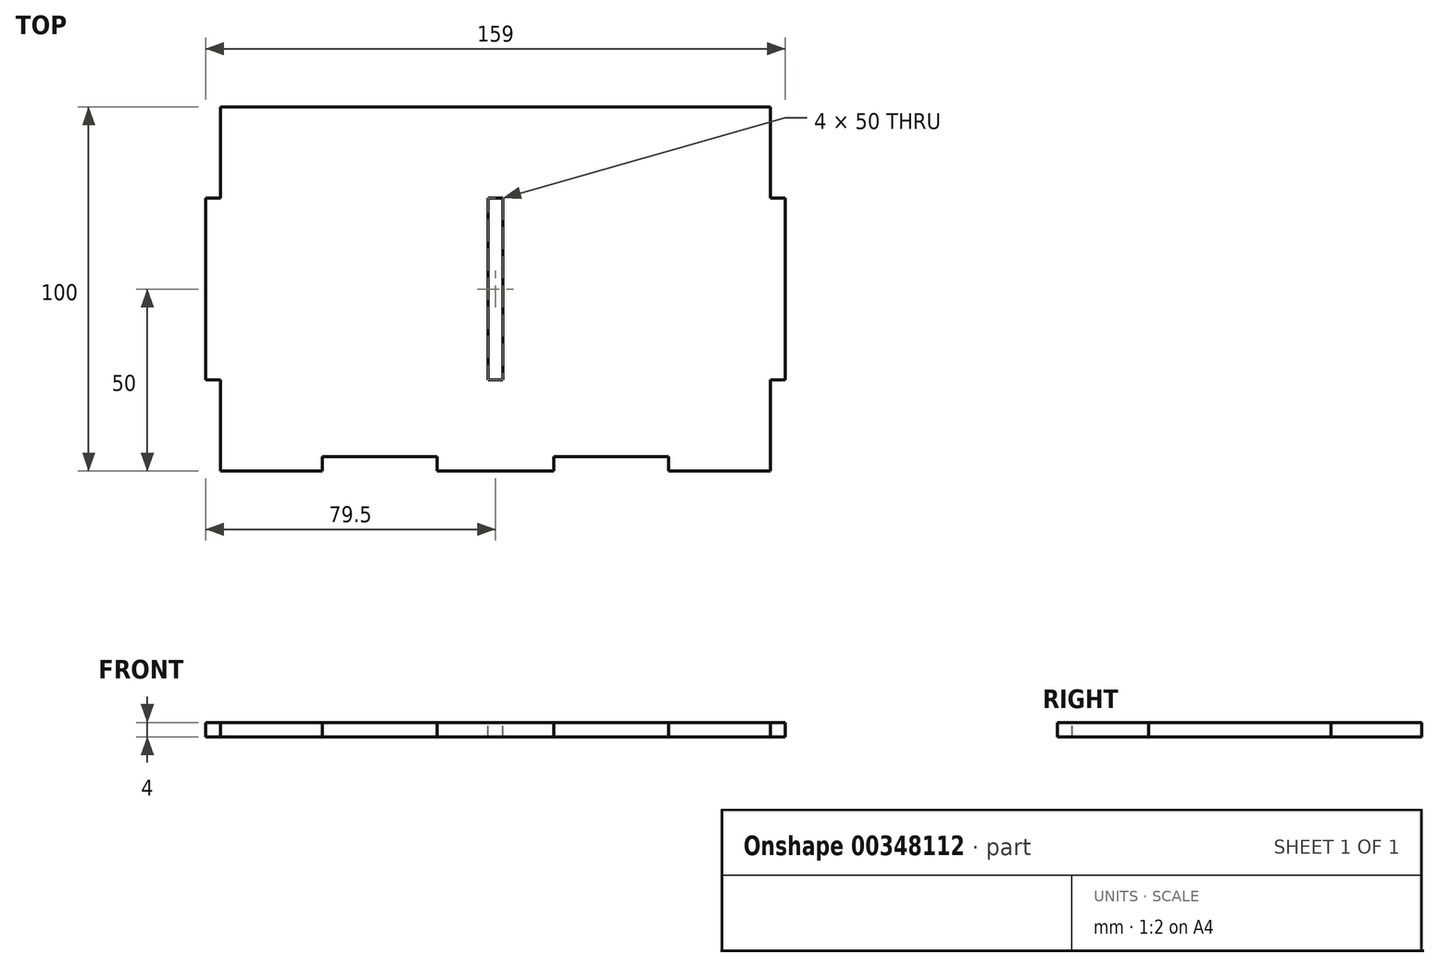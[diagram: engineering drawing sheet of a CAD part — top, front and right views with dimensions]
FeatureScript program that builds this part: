
annotation { "Feature Type Name" : "Feature", "Feature Type Description" : "" }
export const myFeature = defineFeature(function(context is Context, id is Id, definition is map)
    precondition{}
    {
        {
            var Q0;
            Q0=qCreatedBy(makeId("Top.planeOp"),FACE);
            var sketch = newSketch(context, id + "F0", { "sketchPlane" : qUnion([Q0])});
            skLineSegment(sketch, "E0.bottom", {"start": v(0, 0) * mm, "end": v(159, 0) * mm});
            skLineSegment(sketch, "E0.top", {"start": v(0, 100) * mm, "end": v(159, 100) * mm});
            skLineSegment(sketch, "E0.left", {"start": v(0, 0) * mm, "end": v(0, 100) * mm});
            skLineSegment(sketch, "E0.right", {"start": v(159, 0) * mm, "end": v(159, 100) * mm});
            skSolve(sketch);
        }
        {
            var Q0;
            Q0 = qSketchRegion(id + "F0", true);
            extrude(context, id + "F1", {"entities" : qUnion([Q0]), "depth" : 4 * mm});
        }
        {
            var Q0;
            Q0=makeQuery(id+"F1.opExtrude","CAP_FACE",FACE,{"disambiguationData":[OSD([sQuery(id+"F0.wireOp",EDGE,"E0.bottom"),sQuery(id+"F0.wireOp",EDGE,"E0.top"),sQuery(id+"F0.wireOp",EDGE,"E0.left"),sQuery(id+"F0.wireOp",EDGE,"E0.right")])],"isStart":false});
            var sketch = newSketch(context, id + "F2", { "sketchPlane" : qUnion([Q0])});
            skLineSegment(sketch, "E1.bottom", {"start": v(32, 0) * mm, "end": v(63.5, 0) * mm});
            skLineSegment(sketch, "E1.top", {"start": v(32, 4) * mm, "end": v(63.5, 4) * mm});
            skLineSegment(sketch, "E1.left", {"start": v(32, 0) * mm, "end": v(32, 4) * mm});
            skLineSegment(sketch, "E1.right", {"start": v(63.5, 0) * mm, "end": v(63.5, 4) * mm});
            skLineSegment(sketch, "E2.bottom", {"start": v(95.5, 0) * mm, "end": v(127, 0) * mm});
            skLineSegment(sketch, "E2.top", {"start": v(95.5, 4) * mm, "end": v(127, 4) * mm});
            skLineSegment(sketch, "E2.left", {"start": v(95.5, 0) * mm, "end": v(95.5, 4) * mm});
            skLineSegment(sketch, "E2.right", {"start": v(127, 0) * mm, "end": v(127, 4) * mm});
            skSolve(sketch);
        }
        {
            var Q0;
            Q0 = qSketchRegion(id + "F2", true);
            extrude(context, id + "F3", {"entities" : qUnion([Q0]), "operationType" : NewBodyOperationType.REMOVE, "endBound" : BoundingType.UP_TO_NEXT, "oppositeDirection" : true, "depth" : 25 * mm});
        }
        {
            var Q0;
            Q0=makeQuery(id+"F1.opExtrude","CAP_FACE",FACE,{"disambiguationData":[OSD([sQuery(id+"F0.wireOp",EDGE,"E0.bottom"),sQuery(id+"F0.wireOp",EDGE,"E0.top"),sQuery(id+"F0.wireOp",EDGE,"E0.left"),sQuery(id+"F0.wireOp",EDGE,"E0.right")])],"isStart":false});
            var sketch = newSketch(context, id + "F4", { "sketchPlane" : qUnion([Q0])});
            skLineSegment(sketch, "E3.bottom", {"start": v(159, 0) * mm, "end": v(155, 0) * mm});
            skLineSegment(sketch, "E3.top", {"start": v(159, 25) * mm, "end": v(155, 25) * mm});
            skLineSegment(sketch, "E3.left", {"start": v(159, 0) * mm, "end": v(159, 25) * mm});
            skLineSegment(sketch, "E3.right", {"start": v(155, 0) * mm, "end": v(155, 25) * mm});
            skLineSegment(sketch, "E4.bottom", {"start": v(159, 100) * mm, "end": v(155, 100) * mm});
            skLineSegment(sketch, "E4.top", {"start": v(159, 75) * mm, "end": v(155, 75) * mm});
            skLineSegment(sketch, "E4.left", {"start": v(159, 100) * mm, "end": v(159, 75) * mm});
            skLineSegment(sketch, "E4.right", {"start": v(155, 100) * mm, "end": v(155, 75) * mm});
            skLineSegment(sketch, "E5", {"start": v(79.5, 0) * mm, "end": v(79.5, 100) * mm, "construction": true});
            skLineSegment(sketch, "E6.MirrorCS", {"start": v(0, 75) * mm, "end": v(4, 75) * mm});
            skLineSegment(sketch, "E7.MirrorCS", {"start": v(0, 25) * mm, "end": v(4, 25) * mm});
            skLineSegment(sketch, "E8.MirrorCS", {"start": v(0, 0) * mm, "end": v(4, 0) * mm});
            skLineSegment(sketch, "E9.MirrorCS", {"start": v(0, 100) * mm, "end": v(4, 100) * mm});
            skLineSegment(sketch, "E10.MirrorCS", {"start": v(0, 100) * mm, "end": v(0, 75) * mm});
            skLineSegment(sketch, "E11.MirrorCS", {"start": v(4, 100) * mm, "end": v(4, 75) * mm});
            skLineSegment(sketch, "E12.MirrorCS", {"start": v(4, 0) * mm, "end": v(4, 25) * mm});
            skLineSegment(sketch, "E13.MirrorCS", {"start": v(0, 0) * mm, "end": v(0, 25) * mm});
            skSolve(sketch);
        }
        {
            var Q0;
            Q0 = qSketchRegion(id + "F4", true);
            extrude(context, id + "F5", {"entities" : qUnion([Q0]), "operationType" : NewBodyOperationType.REMOVE, "endBound" : BoundingType.UP_TO_NEXT, "oppositeDirection" : true, "depth" : 25 * mm});
        }
        {
            var Q0;
            Q0=makeQuery(id+"F1.opExtrude","CAP_FACE",FACE,{"disambiguationData":[OSD([sQuery(id+"F0.wireOp",EDGE,"E0.bottom"),sQuery(id+"F0.wireOp",EDGE,"E0.top"),sQuery(id+"F0.wireOp",EDGE,"E0.left"),sQuery(id+"F0.wireOp",EDGE,"E0.right")])],"isStart":false});
            var sketch = newSketch(context, id + "F6", { "sketchPlane" : qUnion([Q0])});
            skLineSegment(sketch, "E14.bottom", {"start": v(77.5, 75) * mm, "end": v(81.5, 75) * mm});
            skLineSegment(sketch, "E14.top", {"start": v(77.5, 25) * mm, "end": v(81.5, 25) * mm});
            skLineSegment(sketch, "E14.left", {"start": v(77.5, 75) * mm, "end": v(77.5, 25) * mm});
            skLineSegment(sketch, "E14.right", {"start": v(81.5, 75) * mm, "end": v(81.5, 25) * mm});
            skLineSegment(sketch, "E15", {"start": v(79.5, 0) * mm, "end": v(79.5, 100) * mm, "construction": true});
            skPoint(sketch, "E16", {"position": v(79.5, 75) * mm});
            skSolve(sketch);
        }
        {
            var Q0;
            Q0 = qSketchRegion(id + "F6", true);
            extrude(context, id + "F7", {"entities" : qUnion([Q0]), "operationType" : NewBodyOperationType.REMOVE, "endBound" : BoundingType.UP_TO_NEXT, "oppositeDirection" : true, "depth" : 25 * mm});
        }
    });
